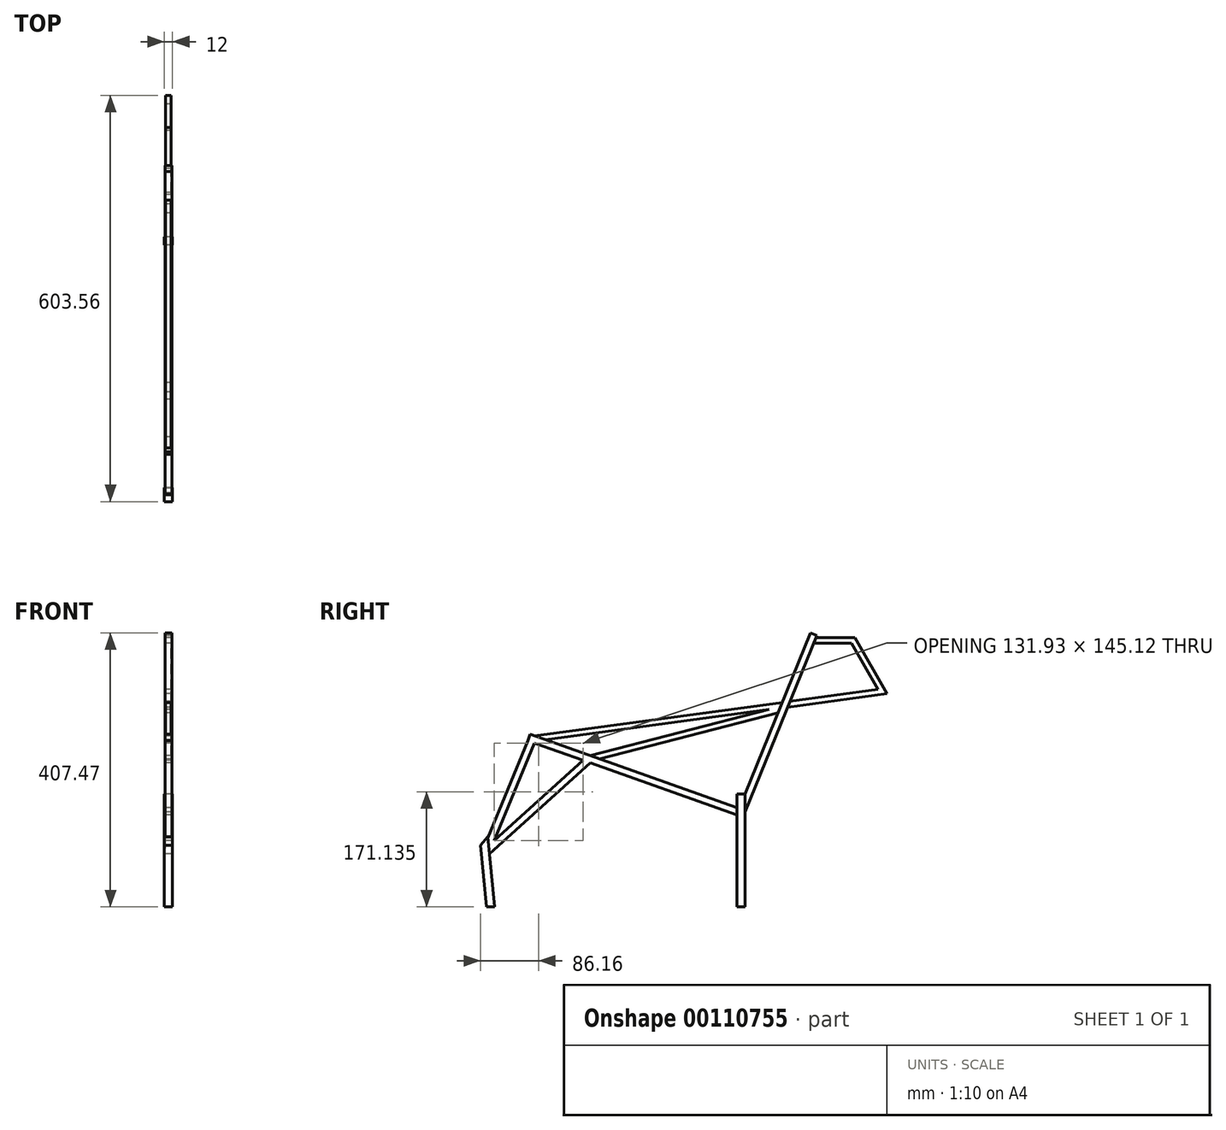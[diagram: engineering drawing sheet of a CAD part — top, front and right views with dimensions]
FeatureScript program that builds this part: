
annotation { "Feature Type Name" : "Feature", "Feature Type Description" : "" }
export const myFeature = defineFeature(function(context is Context, id is Id, definition is map)
    precondition{}
    {
        {
            var Q0;
            Q0=qCreatedBy(makeId("Right.planeOp"),FACE);
            var sketch = newSketch(context, id + "F0", { "sketchPlane" : qUnion([Q0])});
            skLineSegment(sketch, "E0", {"start": v(0, 0) * mm, "end": v(0, 140) * mm});
            skLineSegment(sketch, "E1", {"start": v(0, 140) * mm, "end": v(-310, 250) * mm});
            skLineSegment(sketch, "E2", {"start": v(-310, 250) * mm, "end": v(-380, 80) * mm});
            skLineSegment(sketch, "E3", {"start": v(-380, 80) * mm, "end": v(-372.16, 0) * mm});
            skLineSegment(sketch, "E4", {"start": v(-380, 80) * mm, "end": v(-225.45, 220) * mm});
            skLineSegment(sketch, "E5", {"start": v(-225.45, 220) * mm, "end": v(65.2, 300.5) * mm});
            skLineSegment(sketch, "E6", {"start": v(65.2, 300.5) * mm, "end": v(-310, 250) * mm});
            skLineSegment(sketch, "E7", {"start": v(0, 140) * mm, "end": v(65.2, 300.5) * mm});
            skLineSegment(sketch, "E8", {"start": v(65.2, 300.5) * mm, "end": v(130, 460) * mm});
            skLineSegment(sketch, "E9", {"start": v(130, 460) * mm, "end": v(210, 320) * mm});
            skLineSegment(sketch, "E10", {"start": v(210, 320) * mm, "end": v(65.2, 300.5) * mm});
            skSolve(sketch);
        }
        {
            var Q0;
            Q0=qCreatedBy(makeId("Right.planeOp"),FACE);
            var sketch = newSketch(context, id + "F1", { "sketchPlane" : qUnion([Q0])});
            skLineSegment(sketch, "E11.bottom", {"start": v(-6, 168.05) * mm, "end": v(6, 168.05) * mm});
            skLineSegment(sketch, "E11.top", {"start": v(-6, 0) * mm, "end": v(6, 0) * mm});
            skLineSegment(sketch, "E11.left", {"start": v(-6, 168.05) * mm, "end": v(-6, 0) * mm});
            skLineSegment(sketch, "E11.right", {"start": v(6, 168.05) * mm, "end": v(6, 0) * mm});
            skLineSegment(sketch, "E12", {"start": v(0, 168.05) * mm, "end": v(0, 140) * mm, "construction": true});
            skLineSegment(sketch, "E13", {"start": v(6, 168.05) * mm, "end": v(103.26, 407.47) * mm});
            skLineSegment(sketch, "E14", {"start": v(111.02, 400) * mm, "end": v(168.9, 400) * mm});
            skLineSegment(sketch, "E15", {"start": v(168.9, 400) * mm, "end": v(216.42, 316.83) * mm});
            skLineSegment(sketch, "E16", {"start": v(216.42, 316.83) * mm, "end": v(69.18, 297) * mm});
            skLineSegment(sketch, "E17", {"start": v(69.18, 297) * mm, "end": v(6, 141.48) * mm});
            skLineSegment(sketch, "E18", {"start": v(72.65, 305.55) * mm, "end": v(203.58, 323.17) * mm});
            skLineSegment(sketch, "E19", {"start": v(203.58, 323.17) * mm, "end": v(164.25, 392) * mm});
            skLineSegment(sketch, "E20", {"start": v(164.25, 392) * mm, "end": v(107.77, 392) * mm});
            skLineSegment(sketch, "E21", {"start": v(112.53, 403.7) * mm, "end": v(72.65, 305.55) * mm});
            skLineSegment(sketch, "E22", {"start": v(164.25, 392) * mm, "end": v(168.9, 400) * mm});
            skLineSegment(sketch, "E23", {"start": v(203.58, 323.17) * mm, "end": v(216.42, 316.83) * mm});
            skLineSegment(sketch, "E24", {"start": v(69.18, 297) * mm, "end": v(72.65, 305.55) * mm});
            skLineSegment(sketch, "E25", {"start": v(183.92, 357.59) * mm, "end": v(190.86, 361.56) * mm, "construction": true});
            skLineSegment(sketch, "E26", {"start": v(136.01, 400) * mm, "end": v(136.01, 392) * mm, "construction": true});
            skLineSegment(sketch, "E27", {"start": v(142.8, 306.92) * mm, "end": v(141.73, 314.85) * mm, "construction": true});
            skPoint(sketch, "E28", {"position": v(187.39, 359.57) * mm});
            skPoint(sketch, "E29", {"position": v(142.27, 310.88) * mm});
            skLineSegment(sketch, "E30", {"start": v(112.53, 403.7) * mm, "end": v(103.26, 407.47) * mm});
            skLineSegment(sketch, "E31", {"start": v(-366.13, 0) * mm, "end": v(-378.19, 0) * mm});
            skLineSegment(sketch, "E32", {"start": v(-378.19, 0) * mm, "end": v(-387.14, 91.39) * mm});
            skLineSegment(sketch, "E33", {"start": v(-387.14, 91.39) * mm, "end": v(-376.37, 104.5) * mm});
            skLineSegment(sketch, "E34", {"start": v(-376.37, 104.5) * mm, "end": v(-366.13, 0) * mm});
            skLineSegment(sketch, "E35", {"start": v(-316.62, 247.05) * mm, "end": v(-6, 136.82) * mm});
            skLineSegment(sketch, "E36", {"start": v(-316.62, 247.05) * mm, "end": v(-313.28, 256.47) * mm});
            skLineSegment(sketch, "E37", {"start": v(-313.28, 256.47) * mm, "end": v(-6, 147.43) * mm});
            skLineSegment(sketch, "E38", {"start": v(-314.95, 251.76) * mm, "end": v(-310, 250) * mm, "construction": true});
            skLineSegment(sketch, "E39", {"start": v(107.9, 405.59) * mm, "end": v(130, 460) * mm, "construction": true});
            skLineSegment(sketch, "E40", {"start": v(-373.86, 78.82) * mm, "end": v(-224.31, 214.29) * mm});
            skLineSegment(sketch, "E41", {"start": v(-235.01, 218.09) * mm, "end": v(-375.07, 91.21) * mm});
            skLineSegment(sketch, "E42", {"start": v(61.23, 304) * mm, "end": v(-307.4, 254.39) * mm});
            skLineSegment(sketch, "E43", {"start": v(-290.91, 248.53) * mm, "end": v(57.76, 295.47) * mm});
            skLineSegment(sketch, "E44", {"start": v(-223.97, 224.78) * mm, "end": v(41.72, 293.31) * mm});
            skLineSegment(sketch, "E45", {"start": v(54.91, 288.45) * mm, "end": v(-210.49, 220) * mm});
            skLineSegment(sketch, "E46", {"start": v(-210.49, 220) * mm, "end": v(-212.49, 227.74) * mm, "construction": true});
            skPoint(sketch, "E47", {"position": v(-211.49, 223.87) * mm});
            skLineSegment(sketch, "E48", {"start": v(-235.01, 218.09) * mm, "end": v(-228.3, 210.68) * mm, "construction": true});
            skPoint(sketch, "E49", {"position": v(-231.66, 214.38) * mm});
            skLineSegment(sketch, "E50", {"start": v(-316.62, 247.05) * mm, "end": v(-376.17, 102.43) * mm});
            skLineSegment(sketch, "E51", {"start": v(-366.95, 98.57) * mm, "end": v(-307.19, 243.7) * mm});
            skLineSegment(sketch, "E52", {"start": v(-346.4, 174.74) * mm, "end": v(-337.15, 170.93) * mm, "construction": true});
            skPoint(sketch, "E53", {"position": v(-341.77, 172.84) * mm});
            skSolve(sketch);
        }
        {
            var Q0;
            {var subQ1=sQuery(id+"F1.wireOp",EDGE,"E11.bottom");Q0=makeQuery(id+"F1.imprint","IMPRINT",FACE,{"disambiguationData":[TD([[makeQuery(id+"F1.imprint","IMPRINT",EDGE,{"derivedFrom":subQ1}),-1.0]])]});}
            var Q1;
            {var subQ4=sQuery(id+"F1.wireOp",EDGE,"E31");Q1=makeQuery(id+"F1.imprint","IMPRINT",FACE,{"disambiguationData":[TD([[makeQuery(id+"F1.imprint","IMPRINT",EDGE,{"derivedFrom":subQ4}),-1.0]])]});}
            extrude(context, id + "F2", {"entities" : qUnion([Q0, Q1]), "depth" : 12 * mm, "symmetric" : true});
        }
        {
            var Q0;
            {var subQ1=sQuery(id+"F1.wireOp",EDGE,"E13");Q0=makeQuery(id+"F1.imprint","IMPRINT",FACE,{"disambiguationData":[TD([[makeQuery(id+"F1.imprint","IMPRINT",EDGE,{"derivedFrom":subQ1}),-1.0]])]});}
            var Q1;
            {var subQ4=sQuery(id+"F1.wireOp",EDGE,"E36");Q1=makeQuery(id+"F1.imprint","IMPRINT",FACE,{"disambiguationData":[TD([[makeQuery(id+"F1.imprint","IMPRINT",EDGE,{"derivedFrom":subQ4}),-1.0]])]});}
            var Q2;
            {var subQ4=sQuery(id+"F1.wireOp",EDGE,"E40");Q2=makeQuery(id+"F1.imprint","IMPRINT",FACE,{"disambiguationData":[TD([[makeQuery(id+"F1.imprint","IMPRINT",EDGE,{"derivedFrom":subQ4}),1.0]])]});}
            var Q3;
            {var subQ4=sQuery(id+"F1.wireOp",EDGE,"E50");Q3=makeQuery(id+"F1.imprint","IMPRINT",FACE,{"disambiguationData":[TD([[makeQuery(id+"F1.imprint","IMPRINT",EDGE,{"derivedFrom":subQ4}),1.0]])]});}
            extrude(context, id + "F3", {"entities" : qUnion([Q0, Q1, Q2, Q3]), "operationType" : NewBodyOperationType.ADD, "depth" : 10 * mm, "symmetric" : true});
        }
        {
            var Q0;
            {var subQ4=sQuery(id+"F1.wireOp",EDGE,"E42");Q0=makeQuery(id+"F1.imprint","IMPRINT",FACE,{"disambiguationData":[TD([[makeQuery(id+"F1.imprint","IMPRINT",EDGE,{"derivedFrom":subQ4}),1.0]])]});}
            var Q1;
            {var subQ0=sQuery(id+"F1.wireOp",EDGE,"E44");Q1=makeQuery(id+"F1.imprint","IMPRINT",FACE,{"disambiguationData":[TD([[makeQuery(id+"F1.imprint","IMPRINT",EDGE,{"derivedFrom":subQ0}),-1.0]])]});}
            var Q2;
            Q2=makeQuery(id+"F1.imprint","IMPRINT",FACE,{"disambiguationData":[TD([[makeQuery(id+"F1.imprint","IMPRINT",EDGE,{"derivedFrom":sQuery(id+"F1.wireOp",EDGE,"E16")}),-1.0]])]});
            var Q3;
            Q3=makeQuery(id+"F1.imprint","IMPRINT",FACE,{"disambiguationData":[TD([[makeQuery(id+"F1.imprint","IMPRINT",EDGE,{"derivedFrom":sQuery(id+"F1.wireOp",EDGE,"E15")}),-1.0]])]});
            var Q4;
            {var subQ0=sQuery(id+"F1.wireOp",EDGE,"E14");Q4=makeQuery(id+"F1.imprint","IMPRINT",FACE,{"disambiguationData":[TD([[makeQuery(id+"F1.imprint","IMPRINT",EDGE,{"derivedFrom":subQ0}),-1.0]])]});}
            extrude(context, id + "F4", {"entities" : qUnion([Q0, Q1, Q2, Q3, Q4]), "operationType" : NewBodyOperationType.ADD, "depth" : 8 * mm, "symmetric" : true});
        }
    });
